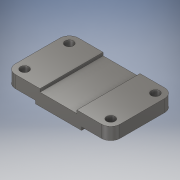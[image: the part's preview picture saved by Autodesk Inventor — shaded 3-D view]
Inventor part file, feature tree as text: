
AUTODESK INVENTOR PART (.ipt)
format: ipt  version: 2019 (Build 230136000, 136)  size: 150,528 bytes
history: native  units: mm
features: extrude x3, sketch x2, fillet x2, mirror x1
ambient origin geometry x8: Origin, YZ Plane, XZ Plane, XY Plane, X Axis, Y Axis, Z Axis, Center Point
bodies: Solid1 (feature_tree)
feature tree (8):
  extrude  "Extrusion1"  Depth=4.0mm
  sketch  "Sketch2"  dims[d2=38.0mm d3=16.0mm d4=44.0mm d5=4.0mm d6=82.0mm d7=0.0mm d8=11.0mm d9=11.0mm d10=12.0mm d11=12.0mm d12=12.0mm d13=12.0mm d14=82.0mm d15=0.0mm d16=82.0mm d17=0.0mm d18=12.0mm d19=12.0mm]
  extrude  "Extrusion2"  Depth=16.0mm
  extrude  "Extrusion3"  Depth=44.0mm
  fillet  "Fillet1"  Radius=4.0mm
  fillet  "Fillet2"  Radius=82.0mm
  mirror  "Mirror1"
  sketch  "Sketch1"  dims[d0=30.0mm d1=4.0mm]
